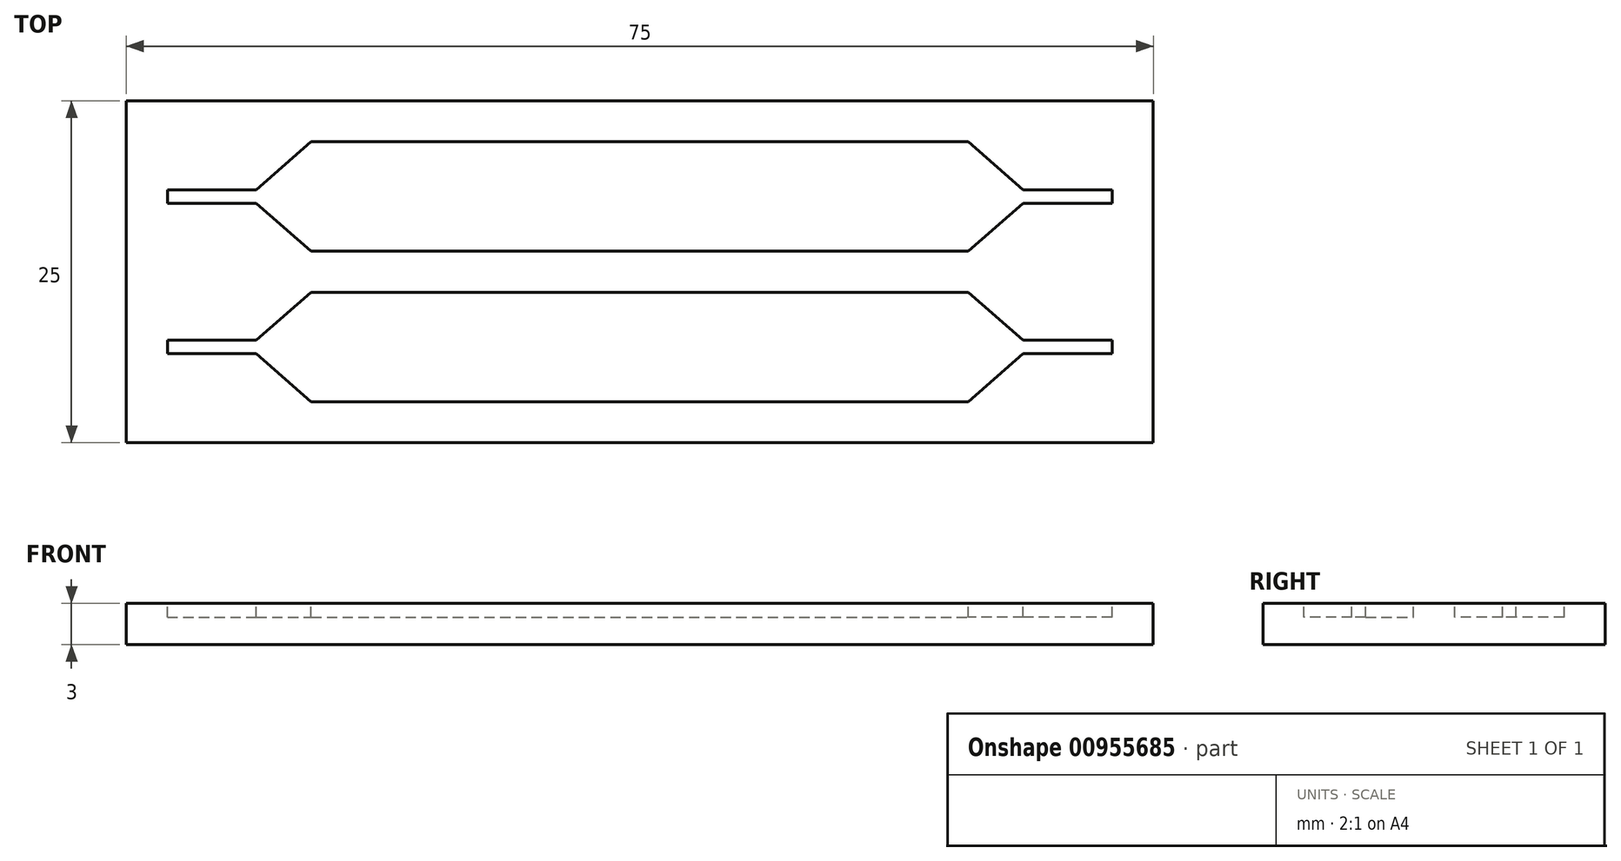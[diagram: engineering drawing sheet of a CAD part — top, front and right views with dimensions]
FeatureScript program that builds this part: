
annotation { "Feature Type Name" : "Feature", "Feature Type Description" : "" }
export const myFeature = defineFeature(function(context is Context, id is Id, definition is map)
    precondition{}
    {
        {
            var Q0;
            Q0=qCreatedBy(makeId("Top.planeOp"),FACE);
            var sketch = newSketch(context, id + "F0", { "sketchPlane" : qUnion([Q0])});
            skLineSegment(sketch, "E0.bottom", {"start": v(-37.84, 12.57) * mm, "end": v(37.16, 12.57) * mm});
            skLineSegment(sketch, "E0.top", {"start": v(-37.84, -12.43) * mm, "end": v(37.16, -12.43) * mm});
            skLineSegment(sketch, "E0.left", {"start": v(-37.84, 12.57) * mm, "end": v(-37.84, -12.43) * mm});
            skLineSegment(sketch, "E0.right", {"start": v(37.16, 12.57) * mm, "end": v(37.16, -12.43) * mm});
            skPoint(sketch, "E1", {"position": v(37.16, 0.07) * mm});
            skPoint(sketch, "E2", {"position": v(-37.84, 0.07) * mm});
            skPoint(sketch, "E3", {"position": v(-37.84, 5.57) * mm});
            skPoint(sketch, "E4", {"position": v(-37.84, -5.43) * mm});
            skPoint(sketch, "E5", {"position": v(37.16, 5.57) * mm});
            skPoint(sketch, "E6", {"position": v(37.16, -5.43) * mm});
            skPoint(sketch, "E7", {"position": v(-34.84, 5.57) * mm});
            skPoint(sketch, "E8", {"position": v(-28.34, 5.57) * mm});
            skPoint(sketch, "E9", {"position": v(-34.84, -5.43) * mm});
            skPoint(sketch, "E10", {"position": v(-28.34, -5.43) * mm});
            skPoint(sketch, "E11", {"position": v(-24.34, 5.57) * mm});
            skPoint(sketch, "E12", {"position": v(-24.34, -5.43) * mm});
            skPoint(sketch, "E13", {"position": v(34.16, 5.57) * mm});
            skPoint(sketch, "E14", {"position": v(27.66, 5.57) * mm});
            skPoint(sketch, "E15", {"position": v(23.66, 5.57) * mm});
            skPoint(sketch, "E16", {"position": v(34.16, -5.43) * mm});
            skPoint(sketch, "E17", {"position": v(27.66, -5.43) * mm});
            skPoint(sketch, "E18", {"position": v(23.66, -5.43) * mm});
            skPoint(sketch, "E19", {"position": v(-34.84, 6.07) * mm});
            skPoint(sketch, "E20", {"position": v(-34.84, 5.07) * mm});
            skPoint(sketch, "E21", {"position": v(-28.34, 5.07) * mm});
            skPoint(sketch, "E22", {"position": v(-28.34, 6.07) * mm});
            skPoint(sketch, "E23", {"position": v(-24.34, 9.57) * mm});
            skPoint(sketch, "E24", {"position": v(-24.34, 1.57) * mm});
            skPoint(sketch, "E25", {"position": v(-34.84, -4.93) * mm});
            skPoint(sketch, "E26", {"position": v(-34.84, -5.93) * mm});
            skPoint(sketch, "E27", {"position": v(-28.34, -5.93) * mm});
            skPoint(sketch, "E28", {"position": v(-28.34, -4.93) * mm});
            skPoint(sketch, "E29", {"position": v(-24.34, -1.43) * mm});
            skPoint(sketch, "E30", {"position": v(-24.34, -9.43) * mm});
            skPoint(sketch, "E31", {"position": v(34.16, -4.93) * mm});
            skPoint(sketch, "E32", {"position": v(34.16, -5.93) * mm});
            skPoint(sketch, "E33", {"position": v(27.66, -4.93) * mm});
            skPoint(sketch, "E34", {"position": v(27.66, -5.93) * mm});
            skPoint(sketch, "E35", {"position": v(23.66, -1.43) * mm});
            skPoint(sketch, "E36", {"position": v(23.66, -9.43) * mm});
            skPoint(sketch, "E37", {"position": v(34.16, 6.07) * mm});
            skPoint(sketch, "E38", {"position": v(34.16, 5.07) * mm});
            skPoint(sketch, "E39", {"position": v(27.66, 6.07) * mm});
            skPoint(sketch, "E40", {"position": v(27.66, 5.07) * mm});
            skPoint(sketch, "E41", {"position": v(23.66, 9.57) * mm});
            skPoint(sketch, "E42", {"position": v(23.66, 1.57) * mm});
            skLineSegment(sketch, "E43", {"start": v(-34.84, 6.07) * mm, "end": v(-28.34, 6.07) * mm});
            skLineSegment(sketch, "E44", {"start": v(-28.34, 6.07) * mm, "end": v(-24.34, 9.57) * mm});
            skLineSegment(sketch, "E45", {"start": v(-34.84, 6.07) * mm, "end": v(-34.84, 5.07) * mm});
            skLineSegment(sketch, "E46", {"start": v(-34.84, 5.07) * mm, "end": v(-28.34, 5.07) * mm});
            skLineSegment(sketch, "E47", {"start": v(-28.34, 5.07) * mm, "end": v(-24.34, 1.57) * mm});
            skLineSegment(sketch, "E48", {"start": v(-24.34, 9.57) * mm, "end": v(23.66, 9.57) * mm});
            skLineSegment(sketch, "E49", {"start": v(-24.34, 1.57) * mm, "end": v(23.66, 1.57) * mm});
            skLineSegment(sketch, "E50", {"start": v(23.66, 9.57) * mm, "end": v(27.66, 6.07) * mm});
            skLineSegment(sketch, "E51", {"start": v(27.66, 6.07) * mm, "end": v(34.16, 6.07) * mm});
            skLineSegment(sketch, "E52", {"start": v(34.16, 6.07) * mm, "end": v(34.16, 5.07) * mm});
            skLineSegment(sketch, "E53", {"start": v(34.16, 5.07) * mm, "end": v(27.66, 5.07) * mm});
            skLineSegment(sketch, "E54", {"start": v(27.66, 5.07) * mm, "end": v(23.66, 1.57) * mm});
            skLineSegment(sketch, "E55", {"start": v(-34.84, -4.93) * mm, "end": v(-28.34, -4.93) * mm});
            skLineSegment(sketch, "E56", {"start": v(-28.34, -4.93) * mm, "end": v(-24.34, -1.43) * mm});
            skLineSegment(sketch, "E57", {"start": v(-34.84, -4.93) * mm, "end": v(-34.84, -5.93) * mm});
            skLineSegment(sketch, "E58", {"start": v(-34.84, -5.93) * mm, "end": v(-28.34, -5.93) * mm});
            skLineSegment(sketch, "E59", {"start": v(-28.34, -5.93) * mm, "end": v(-24.34, -9.43) * mm});
            skLineSegment(sketch, "E60", {"start": v(-24.34, -1.43) * mm, "end": v(23.66, -1.43) * mm});
            skLineSegment(sketch, "E61", {"start": v(-24.34, -9.43) * mm, "end": v(23.66, -9.43) * mm});
            skLineSegment(sketch, "E62", {"start": v(23.66, -1.43) * mm, "end": v(27.66, -4.93) * mm});
            skLineSegment(sketch, "E63", {"start": v(27.66, -4.93) * mm, "end": v(34.16, -4.93) * mm});
            skLineSegment(sketch, "E64", {"start": v(34.16, -4.93) * mm, "end": v(34.16, -5.93) * mm});
            skLineSegment(sketch, "E65", {"start": v(34.16, -5.93) * mm, "end": v(27.66, -5.93) * mm});
            skLineSegment(sketch, "E66", {"start": v(27.66, -5.93) * mm, "end": v(23.66, -9.43) * mm});
            skPoint(sketch, "E67", {"position": v(-33.6, 5.57) * mm});
            skCircle(sketch, "E68", {"center": v(-33.6, 5.57) * mm, "radius": 3.75 * mm});
            skPoint(sketch, "E69", {"position": v(-33.6, -5.43) * mm});
            skCircle(sketch, "E70", {"center": v(-33.6, -5.43) * mm, "radius": 3.75 * mm});
            skPoint(sketch, "E71", {"position": v(32.9, 5.57) * mm});
            skPoint(sketch, "E72", {"position": v(32.9, -5.43) * mm});
            skCircle(sketch, "E73", {"center": v(32.9, 5.57) * mm, "radius": 3.75 * mm});
            skCircle(sketch, "E74", {"center": v(32.9, -5.43) * mm, "radius": 3.75 * mm});
            skCircle(sketch, "E75", {"center": v(-33.6, 5.57) * mm, "radius": 1.75 * mm});
            skCircle(sketch, "E76", {"center": v(-33.6, -5.43) * mm, "radius": 1.75 * mm});
            skCircle(sketch, "E77", {"center": v(32.9, 5.57) * mm, "radius": 1.75 * mm});
            skCircle(sketch, "E78", {"center": v(32.9, -5.43) * mm, "radius": 1.75 * mm});
            skPoint(sketch, "E79", {"position": v(-12.34, 9.57) * mm});
            skPoint(sketch, "E80", {"position": v(-12.34, 1.57) * mm});
            skPoint(sketch, "E81", {"position": v(11.66, 9.57) * mm});
            skPoint(sketch, "E82", {"position": v(11.66, 1.57) * mm});
            skPoint(sketch, "E83", {"position": v(-12.34, -1.43) * mm});
            skPoint(sketch, "E84", {"position": v(-12.34, -9.43) * mm});
            skPoint(sketch, "E85", {"position": v(11.66, -1.43) * mm});
            skPoint(sketch, "E86", {"position": v(11.66, -9.43) * mm});
            skLineSegment(sketch, "E87", {"start": v(-28.34, 6.07) * mm, "end": v(-28.34, 5.07) * mm});
            skLineSegment(sketch, "E88", {"start": v(-28.34, -4.93) * mm, "end": v(-28.34, -5.93) * mm});
            skLineSegment(sketch, "E89", {"start": v(27.66, -4.93) * mm, "end": v(27.66, -5.93) * mm});
            skLineSegment(sketch, "E90", {"start": v(27.66, 6.07) * mm, "end": v(27.66, 5.07) * mm});
            skSolve(sketch);
        }
        {
            var Q0;
            Q0=makeQuery(id+"F0.imprint","IMPRINT",FACE,{"disambiguationData":[TD([[makeQuery(id+"F0.imprint","IMPRINT",EDGE,{"derivedFrom":sQuery(id+"F0.wireOp",EDGE,"E0.bottom")}),-1.0]])]});
            var Q1;
            {var subQ4=sQuery(id+"F0.wireOp",EDGE,"E56");Q1=makeQuery(id+"F0.imprint","IMPRINT",FACE,{"disambiguationData":[TD([[makeQuery(id+"F0.imprint","IMPRINT",EDGE,{"derivedFrom":subQ4}),-1.0]])]});}
            var Q2;
            {var subQ4=sQuery(id+"F0.wireOp",EDGE,"E44");Q2=makeQuery(id+"F0.imprint","IMPRINT",FACE,{"disambiguationData":[TD([[makeQuery(id+"F0.imprint","IMPRINT",EDGE,{"derivedFrom":subQ4}),-1.0]])]});}
            var Q3;
            {var subQ0=sQuery(id+"F0.wireOp",EDGE,"E73");var subQ1=sQuery(id+"F0.wireOp",EDGE,"E51");var subQ2=makeQuery(id+"F0.imprint","INTERSECT",VERTEX,{"derivedFrom":[subQ1,subQ0]});Q3=makeQuery(id+"F0.imprint","IMPRINT",FACE,{"disambiguationData":[TD([[makeQuery(id+"F0.imprint","IMPRINT",EDGE,{"disambiguationData":[TD([[subQ2,-1.0]])],"derivedFrom":subQ1}),1.0]])]});}
            var Q4;
            {var subQ0=sQuery(id+"F0.wireOp",EDGE,"E52");Q4=makeQuery(id+"F0.imprint","IMPRINT",FACE,{"disambiguationData":[TD([[makeQuery(id+"F0.imprint","IMPRINT",EDGE,{"derivedFrom":subQ0}),1.0]])]});}
            var Q5;
            {var subQ0=sQuery(id+"F0.wireOp",EDGE,"E52");Q5=makeQuery(id+"F0.imprint","IMPRINT",FACE,{"disambiguationData":[TD([[makeQuery(id+"F0.imprint","IMPRINT",EDGE,{"derivedFrom":subQ0}),-1.0]])]});}
            var Q6;
            {var subQ0=sQuery(id+"F0.wireOp",EDGE,"E73");var subQ1=sQuery(id+"F0.wireOp",EDGE,"E51");var subQ2=makeQuery(id+"F0.imprint","INTERSECT",VERTEX,{"derivedFrom":[subQ1,subQ0]});Q6=makeQuery(id+"F0.imprint","IMPRINT",FACE,{"disambiguationData":[TD([[makeQuery(id+"F0.imprint","IMPRINT",EDGE,{"disambiguationData":[TD([[subQ2,-1.0]])],"derivedFrom":subQ1}),-1.0]])]});}
            var Q7;
            {var subQ0=sQuery(id+"F0.wireOp",EDGE,"E74");var subQ1=sQuery(id+"F0.wireOp",EDGE,"E63");var subQ2=makeQuery(id+"F0.imprint","INTERSECT",VERTEX,{"derivedFrom":[subQ1,subQ0]});Q7=makeQuery(id+"F0.imprint","IMPRINT",FACE,{"disambiguationData":[TD([[makeQuery(id+"F0.imprint","IMPRINT",EDGE,{"disambiguationData":[TD([[subQ2,-1.0]])],"derivedFrom":subQ1}),1.0]])]});}
            var Q8;
            {var subQ0=sQuery(id+"F0.wireOp",EDGE,"E64");Q8=makeQuery(id+"F0.imprint","IMPRINT",FACE,{"disambiguationData":[TD([[makeQuery(id+"F0.imprint","IMPRINT",EDGE,{"derivedFrom":subQ0}),1.0]])]});}
            var Q9;
            {var subQ0=sQuery(id+"F0.wireOp",EDGE,"E64");Q9=makeQuery(id+"F0.imprint","IMPRINT",FACE,{"disambiguationData":[TD([[makeQuery(id+"F0.imprint","IMPRINT",EDGE,{"derivedFrom":subQ0}),-1.0]])]});}
            var Q10;
            {var subQ0=sQuery(id+"F0.wireOp",EDGE,"E74");var subQ1=sQuery(id+"F0.wireOp",EDGE,"E63");var subQ2=makeQuery(id+"F0.imprint","INTERSECT",VERTEX,{"derivedFrom":[subQ1,subQ0]});Q10=makeQuery(id+"F0.imprint","IMPRINT",FACE,{"disambiguationData":[TD([[makeQuery(id+"F0.imprint","IMPRINT",EDGE,{"disambiguationData":[TD([[subQ2,-1.0]])],"derivedFrom":subQ1}),-1.0]])]});}
            var Q11;
            {var subQ0=sQuery(id+"F0.wireOp",EDGE,"E76");var subQ1=sQuery(id+"F0.wireOp",EDGE,"E55");var subQ2=makeQuery(id+"F0.imprint","INTERSECT",VERTEX,{"derivedFrom":[subQ1,subQ0]});Q11=makeQuery(id+"F0.imprint","IMPRINT",FACE,{"disambiguationData":[TD([[makeQuery(id+"F0.imprint","IMPRINT",EDGE,{"disambiguationData":[TD([[subQ2,-1.0]])],"derivedFrom":subQ1}),1.0]])]});}
            var Q12;
            {var subQ0=sQuery(id+"F0.wireOp",EDGE,"E76");var subQ1=sQuery(id+"F0.wireOp",EDGE,"E55");var subQ2=makeQuery(id+"F0.imprint","INTERSECT",VERTEX,{"derivedFrom":[subQ1,subQ0]});Q12=makeQuery(id+"F0.imprint","IMPRINT",FACE,{"disambiguationData":[TD([[makeQuery(id+"F0.imprint","IMPRINT",EDGE,{"disambiguationData":[TD([[subQ2,-1.0]])],"derivedFrom":subQ1}),-1.0]])]});}
            var Q13;
            {var subQ0=sQuery(id+"F0.wireOp",EDGE,"E57");Q13=makeQuery(id+"F0.imprint","IMPRINT",FACE,{"disambiguationData":[TD([[makeQuery(id+"F0.imprint","IMPRINT",EDGE,{"derivedFrom":subQ0}),-1.0]])]});}
            var Q14;
            {var subQ0=sQuery(id+"F0.wireOp",EDGE,"E57");Q14=makeQuery(id+"F0.imprint","IMPRINT",FACE,{"disambiguationData":[TD([[makeQuery(id+"F0.imprint","IMPRINT",EDGE,{"derivedFrom":subQ0}),1.0]])]});}
            var Q15;
            {var subQ0=sQuery(id+"F0.wireOp",EDGE,"E75");var subQ1=sQuery(id+"F0.wireOp",EDGE,"E43");var subQ2=makeQuery(id+"F0.imprint","INTERSECT",VERTEX,{"derivedFrom":[subQ1,subQ0]});Q15=makeQuery(id+"F0.imprint","IMPRINT",FACE,{"disambiguationData":[TD([[makeQuery(id+"F0.imprint","IMPRINT",EDGE,{"disambiguationData":[TD([[subQ2,-1.0]])],"derivedFrom":subQ1}),1.0]])]});}
            var Q16;
            {var subQ0=sQuery(id+"F0.wireOp",EDGE,"E75");var subQ1=sQuery(id+"F0.wireOp",EDGE,"E43");var subQ2=makeQuery(id+"F0.imprint","INTERSECT",VERTEX,{"derivedFrom":[subQ1,subQ0]});Q16=makeQuery(id+"F0.imprint","IMPRINT",FACE,{"disambiguationData":[TD([[makeQuery(id+"F0.imprint","IMPRINT",EDGE,{"disambiguationData":[TD([[subQ2,-1.0]])],"derivedFrom":subQ1}),-1.0]])]});}
            var Q17;
            {var subQ0=sQuery(id+"F0.wireOp",EDGE,"E45");Q17=makeQuery(id+"F0.imprint","IMPRINT",FACE,{"disambiguationData":[TD([[makeQuery(id+"F0.imprint","IMPRINT",EDGE,{"derivedFrom":subQ0}),-1.0]])]});}
            var Q18;
            {var subQ0=sQuery(id+"F0.wireOp",EDGE,"E45");Q18=makeQuery(id+"F0.imprint","IMPRINT",FACE,{"disambiguationData":[TD([[makeQuery(id+"F0.imprint","IMPRINT",EDGE,{"derivedFrom":subQ0}),1.0]])]});}
            var Q19;
            {var subQ0=sQuery(id+"F0.wireOp",EDGE,"E90");Q19=makeQuery(id+"F0.imprint","IMPRINT",FACE,{"disambiguationData":[TD([[makeQuery(id+"F0.imprint","IMPRINT",EDGE,{"derivedFrom":subQ0}),1.0]])]});}
            var Q20;
            {var subQ0=sQuery(id+"F0.wireOp",EDGE,"E89");Q20=makeQuery(id+"F0.imprint","IMPRINT",FACE,{"disambiguationData":[TD([[makeQuery(id+"F0.imprint","IMPRINT",EDGE,{"derivedFrom":subQ0}),1.0]])]});}
            var Q21;
            {var subQ0=sQuery(id+"F0.wireOp",EDGE,"E87");Q21=makeQuery(id+"F0.imprint","IMPRINT",FACE,{"disambiguationData":[TD([[makeQuery(id+"F0.imprint","IMPRINT",EDGE,{"derivedFrom":subQ0}),-1.0]])]});}
            var Q22;
            {var subQ0=sQuery(id+"F0.wireOp",EDGE,"E88");Q22=makeQuery(id+"F0.imprint","IMPRINT",FACE,{"disambiguationData":[TD([[makeQuery(id+"F0.imprint","IMPRINT",EDGE,{"derivedFrom":subQ0}),-1.0]])]});}
            extrude(context, id + "F1", {"entities" : qUnion([Q0, Q1, Q2, Q3, Q4, Q5, Q6, Q7, Q8, Q9, Q10, Q11, Q12, Q13, Q14, Q15, Q16, Q17, Q18, Q19, Q20, Q21, Q22]), "oppositeDirection" : true, "depth" : 3 * mm, "offsetDistance" : 25 * mm});
        }
        {
            var Q0;
            {var subQ4=sQuery(id+"F0.wireOp",EDGE,"E56");Q0=makeQuery(id+"F0.imprint","IMPRINT",FACE,{"disambiguationData":[TD([[makeQuery(id+"F0.imprint","IMPRINT",EDGE,{"derivedFrom":subQ4}),-1.0]])]});}
            var Q1;
            {var subQ4=sQuery(id+"F0.wireOp",EDGE,"E44");Q1=makeQuery(id+"F0.imprint","IMPRINT",FACE,{"disambiguationData":[TD([[makeQuery(id+"F0.imprint","IMPRINT",EDGE,{"derivedFrom":subQ4}),-1.0]])]});}
            var Q2;
            {var subQ0=sQuery(id+"F0.wireOp",EDGE,"E74");var subQ1=sQuery(id+"F0.wireOp",EDGE,"E63");var subQ2=makeQuery(id+"F0.imprint","INTERSECT",VERTEX,{"derivedFrom":[subQ1,subQ0]});Q2=makeQuery(id+"F0.imprint","IMPRINT",FACE,{"disambiguationData":[TD([[makeQuery(id+"F0.imprint","IMPRINT",EDGE,{"disambiguationData":[TD([[subQ2,-1.0]])],"derivedFrom":subQ1}),-1.0]])]});}
            var Q3;
            {var subQ0=sQuery(id+"F0.wireOp",EDGE,"E64");Q3=makeQuery(id+"F0.imprint","IMPRINT",FACE,{"disambiguationData":[TD([[makeQuery(id+"F0.imprint","IMPRINT",EDGE,{"derivedFrom":subQ0}),-1.0]])]});}
            var Q4;
            {var subQ0=sQuery(id+"F0.wireOp",EDGE,"E73");var subQ1=sQuery(id+"F0.wireOp",EDGE,"E51");var subQ2=makeQuery(id+"F0.imprint","INTERSECT",VERTEX,{"derivedFrom":[subQ1,subQ0]});Q4=makeQuery(id+"F0.imprint","IMPRINT",FACE,{"disambiguationData":[TD([[makeQuery(id+"F0.imprint","IMPRINT",EDGE,{"disambiguationData":[TD([[subQ2,-1.0]])],"derivedFrom":subQ1}),-1.0]])]});}
            var Q5;
            {var subQ0=sQuery(id+"F0.wireOp",EDGE,"E52");Q5=makeQuery(id+"F0.imprint","IMPRINT",FACE,{"disambiguationData":[TD([[makeQuery(id+"F0.imprint","IMPRINT",EDGE,{"derivedFrom":subQ0}),-1.0]])]});}
            var Q6;
            {var subQ0=sQuery(id+"F0.wireOp",EDGE,"E57");Q6=makeQuery(id+"F0.imprint","IMPRINT",FACE,{"disambiguationData":[TD([[makeQuery(id+"F0.imprint","IMPRINT",EDGE,{"derivedFrom":subQ0}),1.0]])]});}
            var Q7;
            {var subQ0=sQuery(id+"F0.wireOp",EDGE,"E76");var subQ1=sQuery(id+"F0.wireOp",EDGE,"E55");var subQ2=makeQuery(id+"F0.imprint","INTERSECT",VERTEX,{"derivedFrom":[subQ1,subQ0]});Q7=makeQuery(id+"F0.imprint","IMPRINT",FACE,{"disambiguationData":[TD([[makeQuery(id+"F0.imprint","IMPRINT",EDGE,{"disambiguationData":[TD([[subQ2,-1.0]])],"derivedFrom":subQ1}),-1.0]])]});}
            var Q8;
            {var subQ0=sQuery(id+"F0.wireOp",EDGE,"E75");var subQ1=sQuery(id+"F0.wireOp",EDGE,"E43");var subQ2=makeQuery(id+"F0.imprint","INTERSECT",VERTEX,{"derivedFrom":[subQ1,subQ0]});Q8=makeQuery(id+"F0.imprint","IMPRINT",FACE,{"disambiguationData":[TD([[makeQuery(id+"F0.imprint","IMPRINT",EDGE,{"disambiguationData":[TD([[subQ2,-1.0]])],"derivedFrom":subQ1}),-1.0]])]});}
            var Q9;
            {var subQ0=sQuery(id+"F0.wireOp",EDGE,"E45");Q9=makeQuery(id+"F0.imprint","IMPRINT",FACE,{"disambiguationData":[TD([[makeQuery(id+"F0.imprint","IMPRINT",EDGE,{"derivedFrom":subQ0}),1.0]])]});}
            var Q10;
            {var subQ0=sQuery(id+"F0.wireOp",EDGE,"E87");Q10=makeQuery(id+"F0.imprint","IMPRINT",FACE,{"disambiguationData":[TD([[makeQuery(id+"F0.imprint","IMPRINT",EDGE,{"derivedFrom":subQ0}),-1.0]])]});}
            var Q11;
            {var subQ0=sQuery(id+"F0.wireOp",EDGE,"E88");Q11=makeQuery(id+"F0.imprint","IMPRINT",FACE,{"disambiguationData":[TD([[makeQuery(id+"F0.imprint","IMPRINT",EDGE,{"derivedFrom":subQ0}),-1.0]])]});}
            var Q12;
            {var subQ0=sQuery(id+"F0.wireOp",EDGE,"E90");Q12=makeQuery(id+"F0.imprint","IMPRINT",FACE,{"disambiguationData":[TD([[makeQuery(id+"F0.imprint","IMPRINT",EDGE,{"derivedFrom":subQ0}),1.0]])]});}
            var Q13;
            {var subQ0=sQuery(id+"F0.wireOp",EDGE,"E89");Q13=makeQuery(id+"F0.imprint","IMPRINT",FACE,{"disambiguationData":[TD([[makeQuery(id+"F0.imprint","IMPRINT",EDGE,{"derivedFrom":subQ0}),1.0]])]});}
            extrude(context, id + "F2", {"entities" : qUnion([Q0, Q1, Q2, Q3, Q4, Q5, Q6, Q7, Q8, Q9, Q10, Q11, Q12, Q13]), "operationType" : NewBodyOperationType.REMOVE, "oppositeDirection" : true, "depth" : 1 * mm, "offsetDistance" : 25 * mm});
        }
    });
